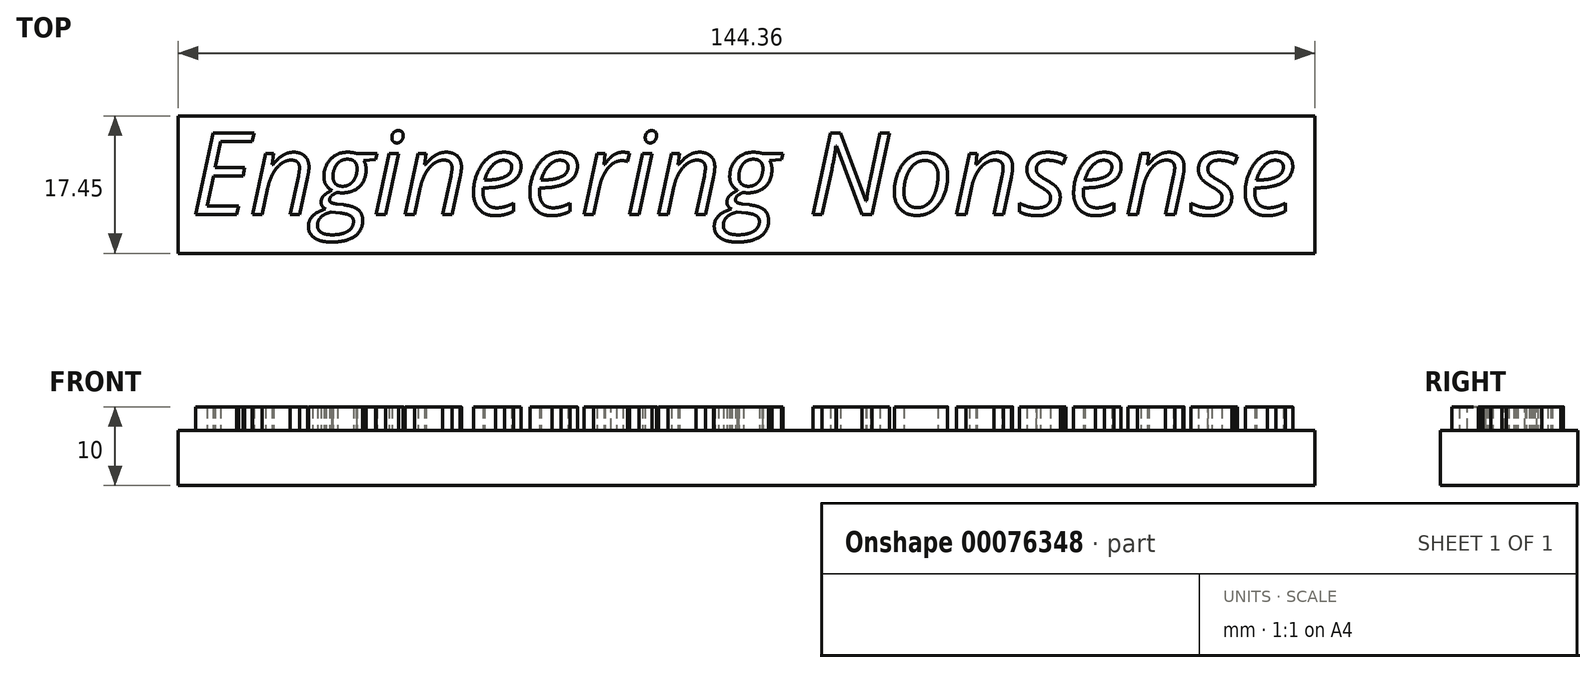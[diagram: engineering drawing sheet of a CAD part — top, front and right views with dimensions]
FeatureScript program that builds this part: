
annotation { "Feature Type Name" : "Feature", "Feature Type Description" : "" }
export const myFeature = defineFeature(function(context is Context, id is Id, definition is map)
    precondition{}
    {
        {
            var Q0;
            Q0=qCreatedBy(makeId("Top.planeOp"),FACE);
            var sketch = newSketch(context, id + "F0", { "sketchPlane" : qUnion([Q0])});
            skText(sketch, "E0", { "text": "Engineering Nonsense", "fontName": "OpenSans-Italic.ttf"});
            const initialGuessF0  = {"E0": [-0.0156, 0.00049, 1, 0, 0.01047]};
            skSetInitialGuess(sketch, initialGuessF0);
            skSolve(sketch);
        }
        {
            var Q0;
            Q0 = qSketchRegion(id + "F0", true);
            extrude(context, id + "F1", {"entities" : qUnion([Q0]), "depth" : 10 * mm});
        }
        {
            var Q0;
            Q0=qCreatedBy(makeId("Top.planeOp"),FACE);
            var sketch = newSketch(context, id + "F2", { "sketchPlane" : qUnion([Q0])});
            skLineSegment(sketch, "E1.bottom", {"start": v(-17.2, 13.02) * mm, "end": v(127.15, 13.02) * mm});
            skLineSegment(sketch, "E1.top", {"start": v(-17.2, -4.43) * mm, "end": v(127.15, -4.43) * mm});
            skLineSegment(sketch, "E1.left", {"start": v(-17.2, 13.02) * mm, "end": v(-17.2, -4.43) * mm});
            skLineSegment(sketch, "E1.right", {"start": v(127.15, 13.02) * mm, "end": v(127.15, -4.43) * mm});
            skSolve(sketch);
        }
        {
            var Q0;
            Q0=makeQuery(id+"F2.imprint","IMPRINT",FACE,{"disambiguationData":[TD([[makeQuery(id+"F2.imprint","IMPRINT",EDGE,{"derivedFrom":sQuery(id+"F2.wireOp",EDGE,"E1.bottom")}),-1.0]])]});
            extrude(context, id + "F3", {"entities" : qUnion([Q0]), "operationType" : NewBodyOperationType.ADD, "depth" : 7 * mm});
        }
    });
